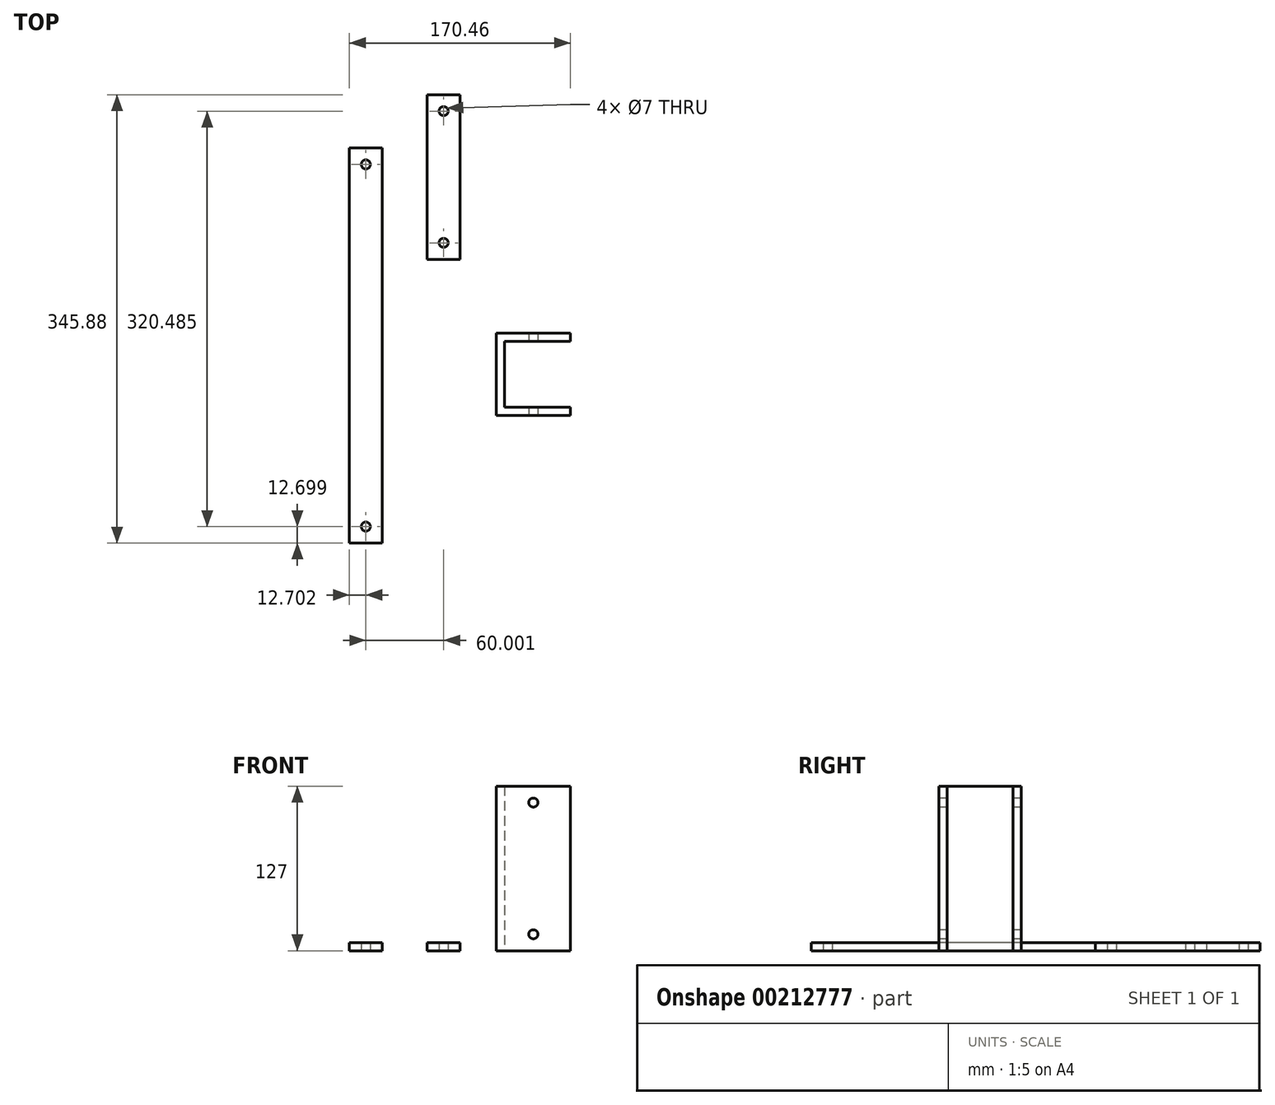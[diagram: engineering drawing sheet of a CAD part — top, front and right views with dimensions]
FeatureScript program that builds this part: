
annotation { "Feature Type Name" : "Feature", "Feature Type Description" : "" }
export const myFeature = defineFeature(function(context is Context, id is Id, definition is map)
    precondition{}
    {
        {
            var Q0;
            Q0=qCreatedBy(makeId("Top.planeOp"),FACE);
            var sketch = newSketch(context, id + "F0", { "sketchPlane" : qUnion([Q0])});
            skLineSegment(sketch, "E0.bottom", {"start": v(-55.06, 231.12) * mm, "end": v(-29.66, 231.12) * mm});
            skLineSegment(sketch, "E0.top", {"start": v(-55.06, -73.68) * mm, "end": v(-29.66, -73.68) * mm});
            skLineSegment(sketch, "E0.left", {"start": v(-55.06, 231.12) * mm, "end": v(-55.06, -73.68) * mm});
            skLineSegment(sketch, "E0.right", {"start": v(-29.66, 231.12) * mm, "end": v(-29.66, -73.68) * mm});
            skLineSegment(sketch, "E1.bottom", {"start": v(4.94, 272.2) * mm, "end": v(30.34, 272.2) * mm});
            skLineSegment(sketch, "E1.top", {"start": v(4.94, 145.2) * mm, "end": v(30.34, 145.2) * mm});
            skLineSegment(sketch, "E1.left", {"start": v(4.94, 272.2) * mm, "end": v(4.94, 145.2) * mm});
            skLineSegment(sketch, "E1.right", {"start": v(30.34, 272.2) * mm, "end": v(30.34, 145.2) * mm});
            skLineSegment(sketch, "E2", {"start": v(58.25, 88.31) * mm, "end": v(58.25, 24.81) * mm});
            skLineSegment(sketch, "E3", {"start": v(58.25, 24.81) * mm, "end": v(115.4, 24.81) * mm});
            skLineSegment(sketch, "E4", {"start": v(115.4, 24.81) * mm, "end": v(115.4, 31.16) * mm});
            skLineSegment(sketch, "E5", {"start": v(115.4, 31.16) * mm, "end": v(64.6, 31.16) * mm});
            skLineSegment(sketch, "E6", {"start": v(64.6, 31.16) * mm, "end": v(64.6, 81.96) * mm});
            skLineSegment(sketch, "E7", {"start": v(64.6, 81.96) * mm, "end": v(115.4, 81.96) * mm});
            skLineSegment(sketch, "E8", {"start": v(115.4, 81.96) * mm, "end": v(115.4, 88.31) * mm});
            skLineSegment(sketch, "E9", {"start": v(115.4, 88.31) * mm, "end": v(58.25, 88.31) * mm});
            skCircle(sketch, "E10", {"center": v(-42.36, 218.42) * mm, "radius": 3.5 * mm});
            skPoint(sketch, "E10.centerSnap0", {"position": v(-42.36, 231.12) * mm});
            skCircle(sketch, "E11", {"center": v(-42.36, -60.98) * mm, "radius": 3.5 * mm});
            skPoint(sketch, "E11.centerSnap0", {"position": v(-42.36, -73.68) * mm});
            skCircle(sketch, "E12", {"center": v(17.64, 259.5) * mm, "radius": 3.5 * mm});
            skPoint(sketch, "E12.centerSnap0", {"position": v(17.64, 272.2) * mm});
            skCircle(sketch, "E13", {"center": v(17.64, 157.9) * mm, "radius": 3.5 * mm});
            skPoint(sketch, "E13.centerSnap0", {"position": v(17.64, 145.2) * mm});
            skSolve(sketch);
        }
        {
            var Q0;
            Q0=makeQuery(id+"F0.imprint","IMPRINT",FACE,{"disambiguationData":[TD([[makeQuery(id+"F0.imprint","IMPRINT",EDGE,{"derivedFrom":sQuery(id+"F0.wireOp",EDGE,"E0.bottom")}),-1.0]])]});
            var Q1;
            Q1=makeQuery(id+"F0.imprint","IMPRINT",FACE,{"disambiguationData":[TD([[makeQuery(id+"F0.imprint","IMPRINT",EDGE,{"derivedFrom":sQuery(id+"F0.wireOp",EDGE,"E1.bottom")}),-1.0]])]});
            extrude(context, id + "F1", {"entities" : qUnion([Q0, Q1]), "depth" : 6.35 * mm});
        }
        {
            var Q0;
            Q0=makeQuery(id+"F0.imprint","IMPRINT",FACE,{"disambiguationData":[TD([[makeQuery(id+"F0.imprint","IMPRINT",EDGE,{"derivedFrom":sQuery(id+"F0.wireOp",EDGE,"E2")}),1.0]])]});
            extrude(context, id + "F2", {"entities" : qUnion([Q0]), "depth" : 127 * mm});
        }
        {
            var Q0;
            Q0=makeQuery(id+"F2.opExtrude","SWEPT_FACE",FACE,{"disambiguationData":[OSD([sQuery(id+"F0.wireOp",EDGE,"E3")])]});
            var sketch = newSketch(context, id + "F3", { "sketchPlane" : qUnion([Q0])});
            skCircle(sketch, "E14", {"center": v(86.83, 12.7) * mm, "radius": 3.5 * mm});
            skPoint(sketch, "E14.centerSnap0", {"position": v(86.83, 0) * mm});
            skCircle(sketch, "E15", {"center": v(86.83, 114.3) * mm, "radius": 3.5 * mm});
            skPoint(sketch, "E15.centerSnap0", {"position": v(86.83, 127) * mm});
            skSolve(sketch);
        }
        {
            var Q0;
            Q0=makeQuery(id+"F3.imprint","IMPRINT",FACE,{"disambiguationData":[TD([[makeQuery(id+"F3.imprint","IMPRINT",EDGE,{"derivedFrom":sQuery(id+"F3.wireOp",EDGE,"E15")}),1.0]])]});
            var Q1;
            Q1=makeQuery(id+"F3.imprint","IMPRINT",FACE,{"disambiguationData":[TD([[makeQuery(id+"F3.imprint","IMPRINT",EDGE,{"derivedFrom":sQuery(id+"F3.wireOp",EDGE,"E14")}),1.0]])]});
            extrude(context, id + "F4", {"entities" : qUnion([Q0, Q1]), "operationType" : NewBodyOperationType.REMOVE, "oppositeDirection" : true, "depth" : 91.44 * mm});
        }
    });
